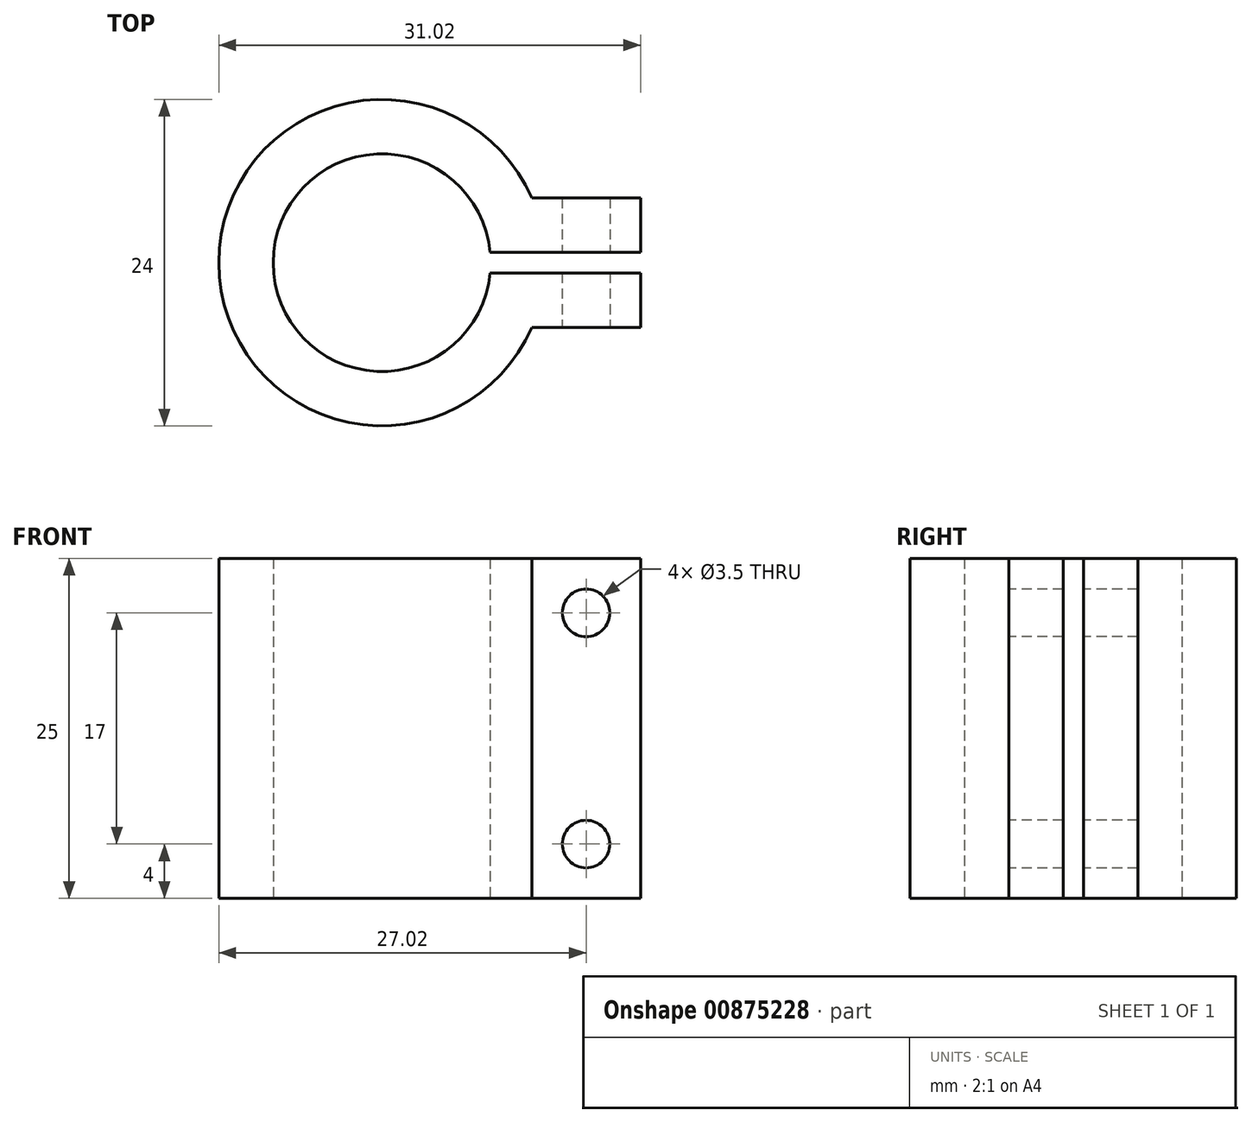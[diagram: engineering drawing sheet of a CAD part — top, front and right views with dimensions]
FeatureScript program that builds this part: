
annotation { "Feature Type Name" : "Feature", "Feature Type Description" : "" }
export const myFeature = defineFeature(function(context is Context, id is Id, definition is map)
    precondition{}
    {
        {
            var Q0;
            Q0=qCreatedBy(makeId("Top.planeOp"),FACE);
            var sketch = newSketch(context, id + "F0", { "sketchPlane" : qUnion([Q0])});
            skArc(sketch, "E0", {"start": v(7.96, 0.75) * mm, "mid": v(-8, 0) * mm, "end": v(7.96, -0.75) * mm});
            skArc(sketch, "E1.0", {"start": v(11.02, 4.75) * mm, "mid": v(-12, 0) * mm, "end": v(11.02, -4.75) * mm});
            skLineSegment(sketch, "E2", {"start": v(0, 0) * mm, "end": v(24.3, 0) * mm, "construction": true});
            skLineSegment(sketch, "E3", {"start": v(7.96, -0.75) * mm, "end": v(19.02, -0.75) * mm});
            skLineSegment(sketch, "E4", {"start": v(11.02, -4.75) * mm, "end": v(19.02, -4.75) * mm});
            skLineSegment(sketch, "E5.MirrorCS", {"start": v(7.96, 0.75) * mm, "end": v(19.02, 0.75) * mm});
            skLineSegment(sketch, "E6.MirrorCS", {"start": v(11.02, 4.75) * mm, "end": v(19.02, 4.75) * mm});
            skLineSegment(sketch, "E7", {"start": v(19.02, 4.75) * mm, "end": v(19.02, 0.75) * mm});
            skLineSegment(sketch, "E8.trimOffspring", {"start": v(19.02, -0.75) * mm, "end": v(19.02, -4.75) * mm});
            skSolve(sketch);
        }
        {
            var Q0;
            Q0 = qSketchRegion(id + "F0", true);
            extrude(context, id + "F1", {"entities" : qUnion([Q0]), "depth" : 25 * mm, "offsetDistance" : 25 * mm});
        }
        {
            var Q0;
            Q0=makeQuery(id+"F1.opExtrude","SWEPT_FACE",FACE,{"disambiguationData":[OSD([sQuery(id+"F0.wireOp",EDGE,"E4")])]});
            var sketch = newSketch(context, id + "F2", { "sketchPlane" : qUnion([Q0])});
            skLineSegment(sketch, "E9", {"start": v(15.02, 0) * mm, "end": v(15.02, 4) * mm, "construction": true});
            skLineSegment(sketch, "E10", {"start": v(15.02, 4) * mm, "end": v(15.02, 21) * mm, "construction": true});
            skLineSegment(sketch, "E11", {"start": v(15.02, 21) * mm, "end": v(15.02, 25) * mm, "construction": true});
            skCircle(sketch, "E12", {"center": v(15.02, 4) * mm, "radius": 1.75 * mm});
            skCircle(sketch, "E13", {"center": v(15.02, 21) * mm, "radius": 1.75 * mm});
            skSolve(sketch);
        }
        {
            var Q0;
            Q0 = qSketchRegion(id + "F2", true);
            var Q1;
            Q1=makeQuery(id+"F1.opExtrude","SWEPT_FACE",FACE,{"disambiguationData":[OSD([sQuery(id+"F0.wireOp",EDGE,"E6.MirrorCS")])]});
            extrude(context, id + "F3", {"entities" : qUnion([Q0]), "operationType" : NewBodyOperationType.REMOVE, "endBound" : BoundingType.UP_TO_SURFACE, "oppositeDirection" : true, "depth" : 25 * mm, "endBoundEntityFace" : qUnion([Q1]), "offsetDistance" : 25 * mm});
        }
    });
